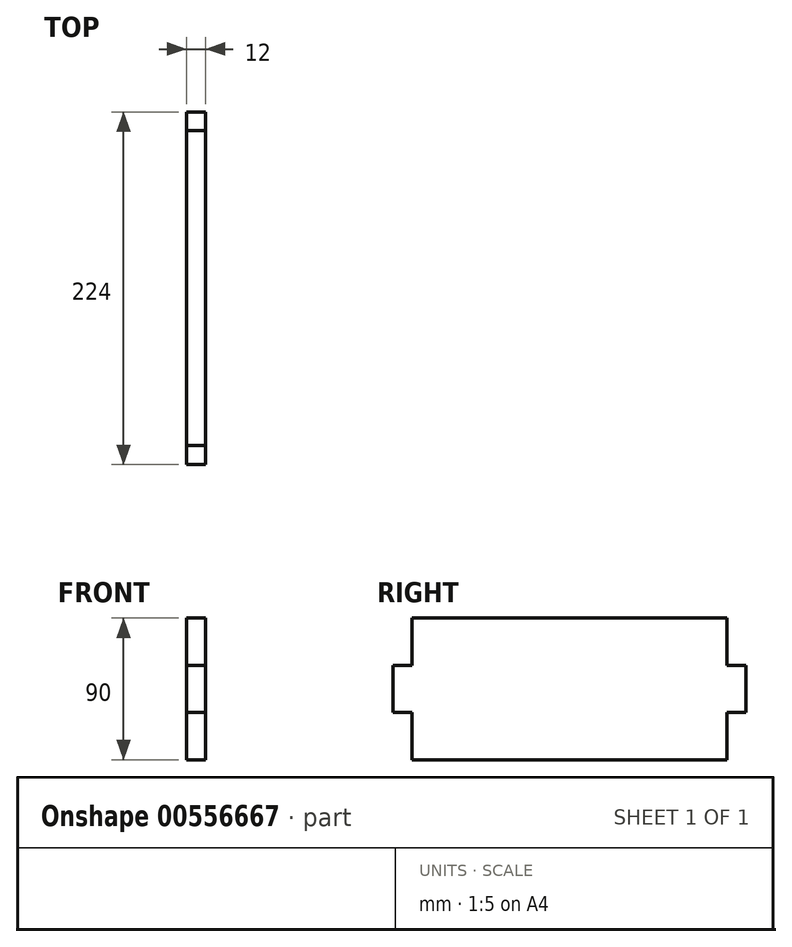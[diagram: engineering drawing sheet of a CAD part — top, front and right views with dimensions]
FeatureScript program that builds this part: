
annotation { "Feature Type Name" : "Feature", "Feature Type Description" : "" }
export const myFeature = defineFeature(function(context is Context, id is Id, definition is map)
    precondition{}
    {
        {
            var Q0;
            Q0=qCreatedBy(makeId("Right.planeOp"),FACE);
            var sketch = newSketch(context, id + "F0", { "sketchPlane" : qUnion([Q0])});
            skLineSegment(sketch, "E0", {"start": v(0, 0) * mm, "end": v(0, 30) * mm});
            skLineSegment(sketch, "E1", {"start": v(0, 30) * mm, "end": v(-12, 30) * mm});
            skLineSegment(sketch, "E2", {"start": v(-12, 30) * mm, "end": v(-12, 60) * mm});
            skLineSegment(sketch, "E3", {"start": v(-12, 60) * mm, "end": v(0, 60) * mm});
            skLineSegment(sketch, "E4", {"start": v(0, 60) * mm, "end": v(0, 90) * mm});
            skLineSegment(sketch, "E5", {"start": v(0, 90) * mm, "end": v(200, 90) * mm});
            skLineSegment(sketch, "E6", {"start": v(200, 90) * mm, "end": v(200, 60) * mm});
            skLineSegment(sketch, "E7", {"start": v(200, 60) * mm, "end": v(212, 60) * mm});
            skLineSegment(sketch, "E8", {"start": v(212, 60) * mm, "end": v(212, 30) * mm});
            skLineSegment(sketch, "E9", {"start": v(212, 30) * mm, "end": v(200, 30) * mm});
            skLineSegment(sketch, "E10", {"start": v(200, 30) * mm, "end": v(200, 0) * mm});
            skLineSegment(sketch, "E11", {"start": v(200, 0) * mm, "end": v(0, 0) * mm});
            skSolve(sketch);
        }
        {
            var Q0;
            Q0=makeQuery(id+"F0.imprint","IMPRINT",FACE,{"disambiguationData":[TD([[makeQuery(id+"F0.imprint","IMPRINT",EDGE,{"derivedFrom":sQuery(id+"F0.wireOp",EDGE,"E0")}),-1.0]])]});
            extrude(context, id + "F1", {"entities" : qUnion([Q0]), "depth" : 12 * mm, "offsetDistance" : 25 * mm});
        }
    });
